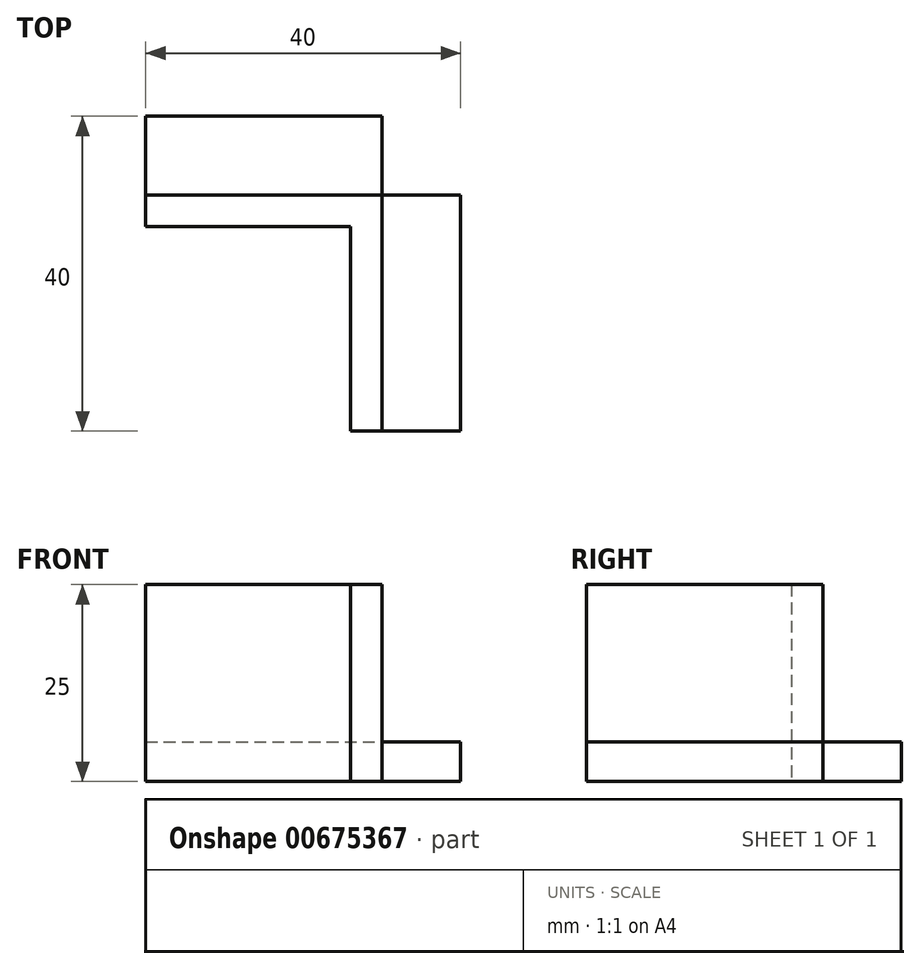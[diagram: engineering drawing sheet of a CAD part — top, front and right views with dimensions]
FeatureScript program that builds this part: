
annotation { "Feature Type Name" : "Feature", "Feature Type Description" : "" }
export const myFeature = defineFeature(function(context is Context, id is Id, definition is map)
    precondition{}
    {
        {
            var Q0;
            Q0=qCreatedBy(makeId("Top.planeOp"),FACE);
            var sketch = newSketch(context, id + "F0", { "sketchPlane" : qUnion([Q0])});
            skLineSegment(sketch, "E0.bottom", {"start": v(0, 0) * mm, "end": v(-14, 0) * mm});
            skLineSegment(sketch, "E0.top", {"start": v(-10, 40) * mm, "end": v(-40, 40) * mm});
            skLineSegment(sketch, "E0.left", {"start": v(0, 0) * mm, "end": v(0, 30) * mm});
            skLineSegment(sketch, "E0.right", {"start": v(-40, 26) * mm, "end": v(-40, 40) * mm});
            skLineSegment(sketch, "E1", {"start": v(-10, 40) * mm, "end": v(-10, 0) * mm});
            skLineSegment(sketch, "E2", {"start": v(-40, 30) * mm, "end": v(-10, 30) * mm});
            skLineSegment(sketch, "E3", {"start": v(-14, 26) * mm, "end": v(-14, 0) * mm});
            skLineSegment(sketch, "E4", {"start": v(-40, 26) * mm, "end": v(-14, 26) * mm});
            skLineSegment(sketch, "E5", {"start": v(-10, 30) * mm, "end": v(0, 30) * mm});
            skSolve(sketch);
        }
        {
            var Q0;
            {var subQ0=sQuery(id+"F0.wireOp",EDGE,"E0.top");Q0=makeQuery(id+"F0.imprint","IMPRINT",FACE,{"disambiguationData":[TD([[makeQuery(id+"F0.imprint","IMPRINT",EDGE,{"derivedFrom":subQ0}),1.0]])]});}
            var Q1;
            {var subQ0=sQuery(id+"F0.wireOp",EDGE,"E0.left");Q1=makeQuery(id+"F0.imprint","IMPRINT",FACE,{"disambiguationData":[TD([[makeQuery(id+"F0.imprint","IMPRINT",EDGE,{"derivedFrom":subQ0}),1.0]])]});}
            extrude(context, id + "F1", {"entities" : qUnion([Q0, Q1]), "depth" : 5 * mm, "offsetDistance" : 25 * mm});
        }
        {
            var Q0;
            {var subQ4=sQuery(id+"F0.wireOp",EDGE,"E2");Q0=makeQuery(id+"F0.imprint","IMPRINT",FACE,{"disambiguationData":[TD([[makeQuery(id+"F0.imprint","IMPRINT",EDGE,{"derivedFrom":subQ4}),-1.0]])]});}
            extrude(context, id + "F2", {"entities" : qUnion([Q0]), "depth" : 25 * mm, "offsetDistance" : 25 * mm});
        }
    });
